# Revit family: Sensor-Lutron-Ceiling_Mount-Occupancy-12ft-LOS-CUS
name_source: partatom
category: Lighting Devices
revit_build: Autodesk Revit 2017 (Build: 20160720_1515(x64)
units: mm (PartAtom-declared; Revit-internal decimal feet)

## family parameters
Cut with Voids When Loaded = No
Host = Face
Maintain Annotation Orientation = Yes
OmniClass Number = 23.85.80.11.27
OmniClass Title = Lighting Controls
Part Type = Normal
Room Calculation Point = No
Round Connector Dimension = Use Diameter
Shared = No

## types (3) — shared parameters
Assembly Code = D5030800
Default Elevation = 0' - 0"
Description = Ultrasonic Ceiling Mount Occupancy Sensor
Instruction Sheet Link = http://www.lutron.com
Manufacturer = Lutron Electronics Co., Inc
Manufacturer Fax Number = 610-282-1243
Nominal Depth = 0' - 1 13/32"
Nominal Length = 0' - 4 1/2"
Nominal Width = 0' - 4 1/2"
Performance URL = http://www.lutron.com
Product Documentation Link = http://www.lutron.com
Product Name = Ultrasonic Ceiling Mount Occupancy Sensor
Product Page URL = http://www.lutron.com
Sensor Material = Plastic-Lutron-White-Gloss
Series = LOS-C
URL = http://www.lutron.com
Version = 2017 - v1.0b
Video Link = https://www.youtube.com
Voltage Comments = 20-24VDC
Warranty URL = http://www.lutron.com
zero-valued in all types: Cost

## per-type parameters (varying)
| type | Coverage | Field of View | Major Motion Offset | Minor Motion Depth | Minor Motion Offset | Rectangular Major Motion Detection | Rectangular Minor Motion Detection |
| LOS-CUS-500-WH | 500.00 SF | 180.00° | 0' - 0" | 16' - 0" | 0' - 0" | 22' - 0" | 16' - 0" |
| LOS-CUS-1000-WH | 1000.00 SF | 180.00° | 0' - 0" | 23' - 0" | 0' - 0" | 32' - 0" | 23' - 0" |
| LOS-CUS-2000-WH | 2000.00 SF | 360.00° | 32' - 0" | 23' - 0" | 22' - 6" | 32' - 0" | 22' - 6" |

note: column(s) folded — value = type name in every type: Model

## geometry (parser evidence)
native form markers: Sweep x3
no freeform markers — native parametric forms only
